# Revit family: JLR_BossDesign_Stng_Toto_HighBack
name_source: partatom
category: Furniture
revit_build: Autodesk Revit 2015 (Build: 20140903_1530(x64)
units: mm (PartAtom-declared; Revit-internal decimal feet)

## types (1)
- Toto High Back
    Assembly Code = E2020200
    AssetType = Movable
    BIMObjectName = JLR_BossDesign_Seating_Toto_HighBack
    Category = Pr_40_50_12 : Chairs, seats and benches
    Color = Grey
    Description = Toto High Back
    DurationUnit = year
    ExpectedLife = 5
    Finish = Leather
    IfcExportAs = IfcFurnishingElementType
    IfcExportType = CHAIR
    Keynote = Pr_40_50_12
    MainColor = Grey
    ManufacturerName = Boss Design
    ManufacturerURL = www.bossdesign.com
    Model = BOS-JLR-F-202
    ModelNumber = BOS-JLR-F-202
    ModelReference = Toto High Back
    NBSDescription = Seating
    NBSReference = 45-35-72/352
    Name = Seating_Toto_HighBack_BossDesign
    NominalHeight = 750 mm  [stored 2.46063 ft]
    NominalLength = 600 mm  [stored 1.9685 ft]
    NominalWidth = 585 mm  [stored 1.91929 ft]
    ProductInformation = www.bossdesign.com/product-list/toto/
    Shape = Rectangular
    Size = 600 x 585 x 750mm
    URL = www.bossdesign.com
    Uniclass2015Code = Pr_40_50_12
    Uniclass2015Title = Chairs, seats and benches
    Uniclass2015Version = Products v1.10
    Version = 1
    WarrantyDescription = Structural Warranty Excludes Foams and Fabrics
    WarrantyDurationLabor = 5
    WarrantyDurationParts = 5
    WarrantyDurationUnit = year

note: [stored X ft] marks values corroborated as IEEE doubles in the binary element streams (Revit-internal decimal feet)

## geometry (parser evidence)
native form markers: Sweep x2
no freeform markers — native parametric forms only
